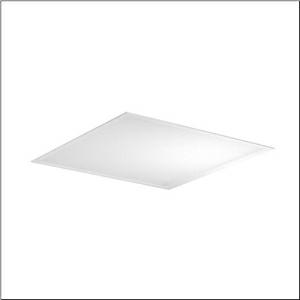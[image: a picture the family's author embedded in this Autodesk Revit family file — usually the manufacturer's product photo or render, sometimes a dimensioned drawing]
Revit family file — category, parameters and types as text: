
# Revit family: apollon_21_square_51mq12wd2414
name_source: partatom
category: Lighting Fixtures
units: mm (PartAtom-declared; Revit-internal decimal feet)

## family parameters
Cut with Voids When Loaded = No
Host = Face
Light Source = No
Part Type = Normal
Room Calculation Point = No
Round Connector Dimension = Use Diameter
Shared = No

## types (1)
- Apollon 21 square (1 x LED, 4200 lm, 24.7 W, 4000K)
    Apparent Load = 25 VA
    CIE Flux Codes = 60 87 97 100 100
    Color Rendering = 80
    Color Temperature = 4000K
    Default Elevation = 1800 mm
    Description = Apollon 21 square, office luminaire, primary optical cover: micro prismatic cover, of PMMA, CAT 2 (L<= 3000cd/m²), light emission: direct distribution, primary light characteristic: symmetric, installation type: lay-in mounting, LED, rated luminous flux: 4.200lm, luminous efficacy: 170lm/W, light colour: 840, colour temperature: 4000K, control gear: DALI 2, Multilumen, with terminal, 5-pole, mains connection: 220..240V, AC/DC, 0/50..60Hz, rated input power: 24.7W, suitable for self-contained emergency lighting element 59MQE002602A with integrated self-test function according to EN 60598-2-22, housing, of aluminium, coated, traffic white (RAL 9016), module: M600, length: 595mm, width: 595mm, height: 55mm, recess depth: 180mm, housing upper side, of sheet steel, galvanised, protection rating (complete): IP20, protection rating (lamp compartment, on room side): IP50, insulation class (complete): insulation class II (safety insulation), certification: CE, ENEC, impact resistance: IK03, permissible operating ambient temperature: -20..+45°C, permissible storage temperature: -40..+80°C, standard: EN 60598-2-22, packaging unit: 1 piece
    Height = 0 mm  [stored 0 ft]
    Lamp = 1 x LED
    Lamp Light Flux = 4200 lm
    Lamp Power = 24.7 W
    Lamp count = 1
    Length = 595 mm
    Luminous efficacy = 170 lm/W
    Manufacturer = Siteco
    ModVariant = No
    Model = 51MQ12WD2414
    Mounting Place = Ceiling
    Mounting Type = Recessed
    Number of Poles = 1
    OnlyDefault = Yes
    Power Factor = 1
    Product Name = Apollon 21 square
    Product group = office luminaire | ceiling recessed
    ProductGroupID = 400
    Protection Class = Protection class II
    Protection Degree = IP 20
    RLX_Detail_Level = 1
    RLX_Emergency_Light_Flux = 0 lm
    RLX_Emergency_Type = 0
    RLX_Emergency_Type_DB = No
    RlxData = <blob elided: 12713 chars, md5=5ccb07d3>
    Socket = socket
    Standby Power = 0 W
    System Light Flux = 4200 lm
    System Power = 25 W
    Type Comments = Product without accessories
    Type Image = l_1291049.jpg
    URL = http://relux.com
    VarID = ---
    Voltage = 0 V
    Weight = 0.00 kg
    Width = 595 mm

note: [stored X ft] marks values corroborated as IEEE doubles in the binary element streams (Revit-internal decimal feet)

## geometry (parser evidence)
native form markers: Sweep x12
no freeform markers — native parametric forms only
